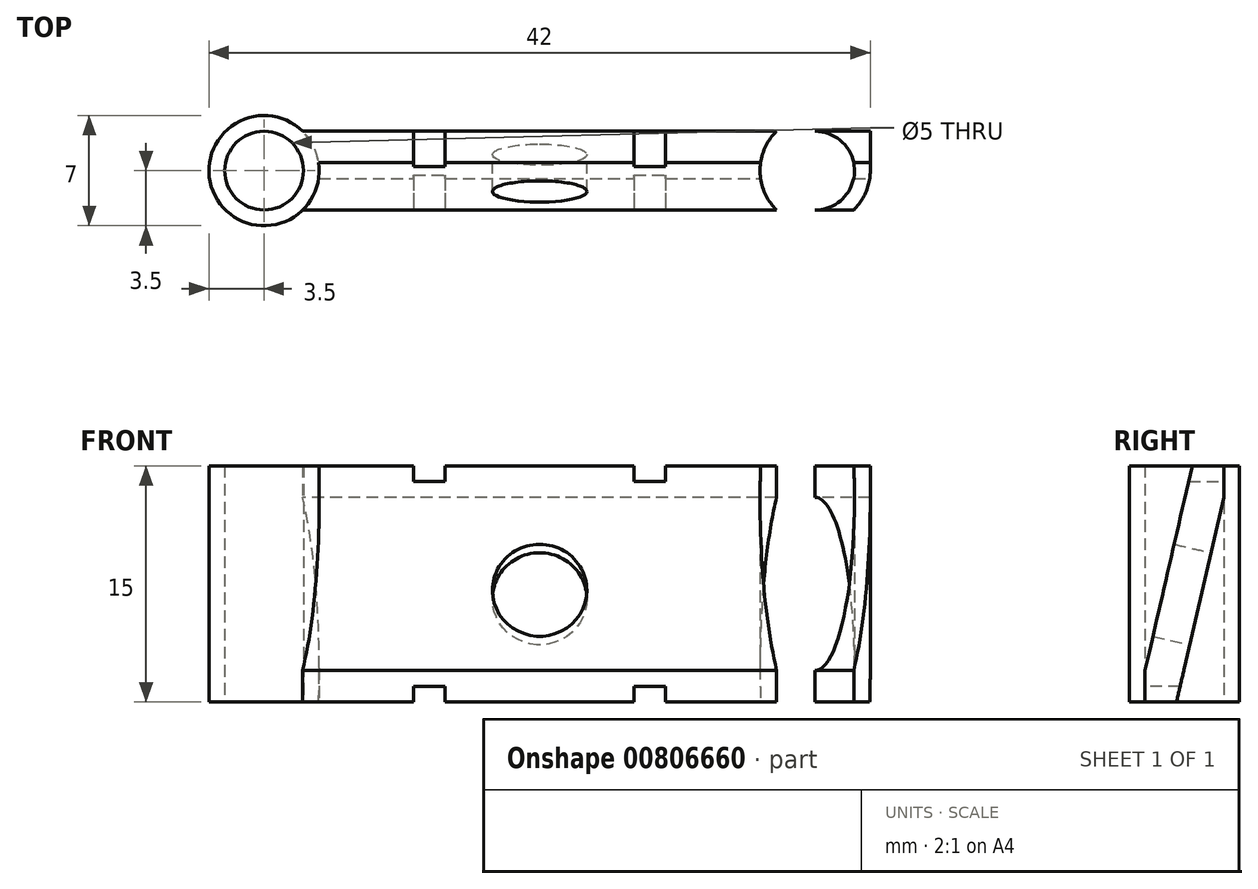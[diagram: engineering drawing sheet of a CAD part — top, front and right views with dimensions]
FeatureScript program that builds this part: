
annotation { "Feature Type Name" : "Feature", "Feature Type Description" : "" }
export const myFeature = defineFeature(function(context is Context, id is Id, definition is map)
    precondition{}
    {
        {
            var Q0;
            Q0=qCreatedBy(makeId("Top.planeOp"),FACE);
            var sketch = newSketch(context, id + "F0", { "sketchPlane" : qUnion([Q0])});
            skLineSegment(sketch, "E0.bottom", {"start": v(21, 2.5) * mm, "end": v(-21, 2.5) * mm});
            skLineSegment(sketch, "E0.top", {"start": v(21, -2.5) * mm, "end": v(-21, -2.5) * mm});
            skLineSegment(sketch, "E0.left", {"start": v(21, 2.5) * mm, "end": v(21, -2.5) * mm});
            skLineSegment(sketch, "E0.right", {"start": v(-21, 2.5) * mm, "end": v(-21, -2.5) * mm});
            skPoint(sketch, "E0.middle", {"position": v(0, 0) * mm});
            skLineSegment(sketch, "E1", {"start": v(-21, 0) * mm, "end": v(21, 0) * mm, "construction": true});
            skLineSegment(sketch, "E2", {"start": v(0, 2.5) * mm, "end": v(0, -2.5) * mm, "construction": true});
            skCircle(sketch, "E3", {"center": v(-17.5, 0) * mm, "radius": 3.5 * mm});
            skCircle(sketch, "E4.MirrorC", {"center": v(17.5, 0) * mm, "radius": 3.5 * mm});
            skCircle(sketch, "E5", {"center": v(-17.5, 0) * mm, "radius": 2.5 * mm});
            skCircle(sketch, "E6.MirrorC", {"center": v(17.5, 0) * mm, "radius": 2.5 * mm});
            skSolve(sketch);
        }
        {
            var Q0;
            {var subQ0=sQuery(id+"F0.wireOp",EDGE,"E3");var subQ1=sQuery(id+"F0.wireOp",EDGE,"E0.bottom");var subQ2=makeQuery(id+"F0.imprint","INTERSECT",VERTEX,{"disambiguationData":[OD(0.0)],"derivedFrom":[subQ1,subQ0]});Q0=makeQuery(id+"F0.imprint","IMPRINT",FACE,{"disambiguationData":[TD([[makeQuery(id+"F0.imprint","IMPRINT",EDGE,{"disambiguationData":[TD([[subQ2,-1.0]])],"derivedFrom":subQ1}),-1.0]])]});}
            var Q1;
            {var subQ0=sQuery(id+"F0.wireOp",EDGE,"E3");var subQ1=sQuery(id+"F0.wireOp",EDGE,"E0.bottom");var subQ2=makeQuery(id+"F0.imprint","INTERSECT",VERTEX,{"disambiguationData":[OD(1.0)],"derivedFrom":[subQ1,subQ0]});Q1=makeQuery(id+"F0.imprint","IMPRINT",FACE,{"disambiguationData":[TD([[makeQuery(id+"F0.imprint","IMPRINT",EDGE,{"disambiguationData":[TD([[subQ2,1.0]])],"derivedFrom":subQ1}),1.0]])]});}
            var Q2;
            {var subQ0=sQuery(id+"F0.wireOp",EDGE,"E3");var subQ1=sQuery(id+"F0.wireOp",EDGE,"E0.top");var subQ2=makeQuery(id+"F0.imprint","INTERSECT",VERTEX,{"disambiguationData":[OD(0.0)],"derivedFrom":[subQ1,subQ0]});Q2=makeQuery(id+"F0.imprint","IMPRINT",FACE,{"disambiguationData":[TD([[makeQuery(id+"F0.imprint","IMPRINT",EDGE,{"disambiguationData":[TD([[subQ2,-1.0]])],"derivedFrom":subQ1}),1.0]])]});}
            var Q3;
            {var subQ0=sQuery(id+"F0.wireOp",EDGE,"E3");var subQ1=sQuery(id+"F0.wireOp",EDGE,"E0.bottom");var subQ2=makeQuery(id+"F0.imprint","INTERSECT",VERTEX,{"disambiguationData":[OD(0.0)],"derivedFrom":[subQ1,subQ0]});Q3=makeQuery(id+"F0.imprint","IMPRINT",FACE,{"disambiguationData":[TD([[makeQuery(id+"F0.imprint","IMPRINT",EDGE,{"disambiguationData":[TD([[subQ2,-1.0]])],"derivedFrom":subQ1}),1.0]])]});}
            var Q4;
            {var subQ0=sQuery(id+"F0.wireOp",EDGE,"E4.MirrorC");var subQ1=sQuery(id+"F0.wireOp",EDGE,"E0.bottom");var subQ2=makeQuery(id+"F0.imprint","INTERSECT",VERTEX,{"disambiguationData":[OD(1.0)],"derivedFrom":[subQ1,subQ0]});Q4=makeQuery(id+"F0.imprint","IMPRINT",FACE,{"disambiguationData":[TD([[makeQuery(id+"F0.imprint","IMPRINT",EDGE,{"disambiguationData":[TD([[subQ2,-1.0]])],"derivedFrom":subQ1}),1.0]])]});}
            var Q5;
            {var subQ0=sQuery(id+"F0.wireOp",EDGE,"E4.MirrorC");var subQ1=sQuery(id+"F0.wireOp",EDGE,"E0.bottom");var subQ2=makeQuery(id+"F0.imprint","INTERSECT",VERTEX,{"disambiguationData":[OD(1.0)],"derivedFrom":[subQ1,subQ0]});Q5=makeQuery(id+"F0.imprint","IMPRINT",FACE,{"disambiguationData":[TD([[makeQuery(id+"F0.imprint","IMPRINT",EDGE,{"disambiguationData":[TD([[subQ2,1.0]])],"derivedFrom":subQ1}),1.0]])]});}
            var Q6;
            {var subQ0=sQuery(id+"F0.wireOp",EDGE,"E4.MirrorC");var subQ1=sQuery(id+"F0.wireOp",EDGE,"E0.bottom");var subQ2=makeQuery(id+"F0.imprint","INTERSECT",VERTEX,{"disambiguationData":[OD(0.0)],"derivedFrom":[subQ1,subQ0]});Q6=makeQuery(id+"F0.imprint","IMPRINT",FACE,{"disambiguationData":[TD([[makeQuery(id+"F0.imprint","IMPRINT",EDGE,{"disambiguationData":[TD([[subQ2,-1.0]])],"derivedFrom":subQ1}),-1.0]])]});}
            var Q7;
            {var subQ0=sQuery(id+"F0.wireOp",EDGE,"E4.MirrorC");var subQ4=sQuery(id+"F0.wireOp",EDGE,"E0.bottom");var subQ5=makeQuery(id+"F0.imprint","INTERSECT",VERTEX,{"disambiguationData":[OD(0.0)],"derivedFrom":[subQ4,subQ0]});Q7=makeQuery(id+"F0.imprint","IMPRINT",FACE,{"disambiguationData":[TD([[makeQuery(id+"F0.imprint","IMPRINT",EDGE,{"disambiguationData":[TD([[subQ5,-1.0]])],"derivedFrom":subQ4}),1.0]])]});}
            var Q8;
            {var subQ0=sQuery(id+"F0.wireOp",EDGE,"E4.MirrorC");var subQ1=sQuery(id+"F0.wireOp",EDGE,"E0.top");var subQ2=makeQuery(id+"F0.imprint","INTERSECT",VERTEX,{"disambiguationData":[OD(0.0)],"derivedFrom":[subQ1,subQ0]});Q8=makeQuery(id+"F0.imprint","IMPRINT",FACE,{"disambiguationData":[TD([[makeQuery(id+"F0.imprint","IMPRINT",EDGE,{"disambiguationData":[TD([[subQ2,-1.0]])],"derivedFrom":subQ1}),1.0]])]});}
            extrude(context, id + "F1", {"entities" : qUnion([Q0, Q1, Q2, Q3, Q4, Q5, Q6, Q7, Q8]), "depth" : 15 * mm, "offsetDistance" : 25 * mm});
        }
        {
            var Q0;
            Q0=makeQuery(id+"F1.opExtrude","CAP_EDGE",EDGE,{"disambiguationData":[OSD([sQuery(id+"F0.wireOp",EDGE,"E0.top")])],"isStart":false});
            chamfer(context, id + "F2", {"entities" : qUnion([Q0]), "chamferType" : ChamferType.TWO_OFFSETS, "width1" : 13 * mm, "oppositeDirection" : false, "width2" : 3 * mm, "tangentPropagation" : true});
        }
        {
            var Q0;
            Q0=makeQuery(id+"F1.opExtrude","CAP_EDGE",EDGE,{"disambiguationData":[OSD([sQuery(id+"F0.wireOp",EDGE,"E0.bottom")])],"isStart":true});
            chamfer(context, id + "F3", {"entities" : qUnion([Q0]), "chamferType" : ChamferType.TWO_OFFSETS, "width1" : 13 * mm, "oppositeDirection" : false, "width2" : 3 * mm, "tangentPropagation" : true});
        }
        {
            var Q0;
            Q0=makeQuery(id+"F3.opChamfer","BLEND_FACE",FACE,{"disambiguationData":[OSD([sQuery(id+"F0.wireOp",EDGE,"E0.bottom")])]});
            var sketch = newSketch(context, id + "F4", { "sketchPlane" : qUnion([Q0])});
            skLineSegment(sketch, "E7", {"start": v(0, 13.23) * mm, "end": v(0, 0) * mm, "construction": true});
            skCircle(sketch, "E8", {"center": v(0, 6.61) * mm, "radius": 3 * mm});
            skSolve(sketch);
        }
        {
            var Q0;
            Q0=makeQuery(id+"F4.imprint","IMPRINT",FACE,{"disambiguationData":[TD([[makeQuery(id+"F4.imprint","IMPRINT",EDGE,{"derivedFrom":sQuery(id+"F4.wireOp",EDGE,"E8")}),1.0]])]});
            extrude(context, id + "F5", {"entities" : qUnion([Q0]), "operationType" : NewBodyOperationType.REMOVE, "oppositeDirection" : true, "depth" : 25 * mm, "offsetDistance" : 25 * mm});
        }
        {
            var Q0;
            Q0=makeQuery(id+"F1.opExtrude","CAP_FACE",FACE,{"disambiguationData":[OSD([sQuery(id+"F0.wireOp",EDGE,"E0.bottom"),sQuery(id+"F0.wireOp",EDGE,"E0.top"),sQuery(id+"F0.wireOp",EDGE,"E3"),sQuery(id+"F0.wireOp",EDGE,"E4.MirrorC"),sQuery(id+"F0.wireOp",EDGE,"E5"),sQuery(id+"F0.wireOp",EDGE,"E6.MirrorC")])],"isStart":false});
            var sketch = newSketch(context, id + "F6", { "sketchPlane" : qUnion([Q0])});
            skLineSegment(sketch, "E9", {"start": v(0, 0.5) * mm, "end": v(0, 2.5) * mm, "construction": true});
            skLineSegment(sketch, "E10.bottom", {"start": v(8, 0) * mm, "end": v(6, 0) * mm});
            skLineSegment(sketch, "E10.top", {"start": v(8, 3) * mm, "end": v(6, 3) * mm});
            skLineSegment(sketch, "E10.left", {"start": v(8, 0) * mm, "end": v(8, 3) * mm});
            skLineSegment(sketch, "E10.right", {"start": v(6, 0) * mm, "end": v(6, 3) * mm});
            skLineSegment(sketch, "E11.MirrorCS", {"start": v(-6, 0) * mm, "end": v(-6, 3) * mm});
            skLineSegment(sketch, "E12.MirrorCS", {"start": v(-8, 0) * mm, "end": v(-8, 3) * mm});
            skLineSegment(sketch, "E13.MirrorCS", {"start": v(-8, 3) * mm, "end": v(-6, 3) * mm});
            skLineSegment(sketch, "E14.MirrorCS", {"start": v(-8, 0) * mm, "end": v(-6, 0) * mm});
            skLineSegment(sketch, "E15", {"start": v(8, 1.5) * mm, "end": v(6, 1.5) * mm, "construction": true});
            skLineSegment(sketch, "E16", {"start": v(0, 1.5) * mm, "end": v(14.82, 1.5) * mm, "construction": true});
            skSolve(sketch);
        }
        {
            var Q0;
            Q0=makeQuery(id+"F6.imprint","IMPRINT",FACE,{"disambiguationData":[TD([[makeQuery(id+"F6.imprint","IMPRINT",EDGE,{"derivedFrom":sQuery(id+"F6.wireOp",EDGE,"E10.bottom")}),1.0]])]});
            var Q1;
            Q1=makeQuery(id+"F6.imprint","IMPRINT",FACE,{"disambiguationData":[TD([[makeQuery(id+"F6.imprint","IMPRINT",EDGE,{"derivedFrom":sQuery(id+"F6.wireOp",EDGE,"E11.MirrorCS")}),1.0]])]});
            var Q2;
            {var subQ0=sQuery(id+"F6.wireOp",EDGE,"E10.left");var subQ2=sQuery(id+"F0.wireOp",EDGE,"E0.bottom");var subQ5=makeQuery(id+"F1.opExtrude","CAP_EDGE",EDGE,{"disambiguationData":[OSD([subQ2])],"isStart":false});var subQ6=makeQuery(id+"F6.imprint","INTERSECT",VERTEX,{"derivedFrom":[subQ5,subQ0]});Q2=makeQuery(id+"F6.imprint","IMPRINT",FACE,{"disambiguationData":[TD([[makeQuery(id+"F6.imprint","IMPRINT",EDGE,{"disambiguationData":[TD([[subQ6,-1.0]])],"derivedFrom":subQ5}),1.0]])]});}
            var Q3;
            {var subQ0=sQuery(id+"F6.wireOp",EDGE,"E10.bottom");Q3=makeQuery(id+"F6.imprint","IMPRINT",FACE,{"disambiguationData":[TD([[makeQuery(id+"F6.imprint","IMPRINT",EDGE,{"derivedFrom":subQ0}),-1.0]])]});}
            var Q4;
            {var subQ0=sQuery(id+"F6.wireOp",EDGE,"E10.top");Q4=makeQuery(id+"F6.imprint","IMPRINT",FACE,{"disambiguationData":[TD([[makeQuery(id+"F6.imprint","IMPRINT",EDGE,{"derivedFrom":subQ0}),1.0]])]});}
            extrude(context, id + "F7", {"entities" : qUnion([Q0, Q1, Q2, Q3, Q4]), "operationType" : NewBodyOperationType.REMOVE, "oppositeDirection" : true, "depth" : 1 * mm, "offsetDistance" : 25 * mm});
        }
        {
            var Q0;
            Q0=makeQuery(id+"F1.opExtrude","CAP_FACE",FACE,{"disambiguationData":[OSD([sQuery(id+"F0.wireOp",EDGE,"E0.bottom"),sQuery(id+"F0.wireOp",EDGE,"E0.top"),sQuery(id+"F0.wireOp",EDGE,"E3"),sQuery(id+"F0.wireOp",EDGE,"E4.MirrorC"),sQuery(id+"F0.wireOp",EDGE,"E5"),sQuery(id+"F0.wireOp",EDGE,"E6.MirrorC")])],"isStart":true});
            var sketch = newSketch(context, id + "F8", { "sketchPlane" : qUnion([Q0])});
            skLineSegment(sketch, "E17", {"start": v(0, 0.5) * mm, "end": v(0, 2.5) * mm, "construction": true});
            skLineSegment(sketch, "E18", {"start": v(0, 1.5) * mm, "end": v(15.17, 1.5) * mm, "construction": true});
            skLineSegment(sketch, "E19.bottom", {"start": v(8, 0) * mm, "end": v(6, 0) * mm});
            skLineSegment(sketch, "E19.top", {"start": v(8, 3) * mm, "end": v(6, 3) * mm});
            skLineSegment(sketch, "E19.left", {"start": v(8, 0) * mm, "end": v(8, 3) * mm});
            skLineSegment(sketch, "E19.right", {"start": v(6, 0) * mm, "end": v(6, 3) * mm});
            skLineSegment(sketch, "E20", {"start": v(8, 1.5) * mm, "end": v(6, 1.5) * mm, "construction": true});
            skLineSegment(sketch, "E21.MirrorCS", {"start": v(-8, 1.5) * mm, "end": v(-6, 1.5) * mm, "construction": true});
            skLineSegment(sketch, "E22.MirrorCS", {"start": v(-8, 0) * mm, "end": v(-6, 0) * mm});
            skLineSegment(sketch, "E23.MirrorCS", {"start": v(-8, 0) * mm, "end": v(-8, 3) * mm});
            skLineSegment(sketch, "E24.MirrorCS", {"start": v(-6, 0) * mm, "end": v(-6, 3) * mm});
            skLineSegment(sketch, "E25.MirrorCS", {"start": v(-8, 3) * mm, "end": v(-6, 3) * mm});
            skSolve(sketch);
        }
        {
            var Q0;
            {var subQ0=sQuery(id+"F8.wireOp",EDGE,"E19.bottom");Q0=makeQuery(id+"F8.imprint","IMPRINT",FACE,{"disambiguationData":[TD([[makeQuery(id+"F8.imprint","IMPRINT",EDGE,{"derivedFrom":subQ0}),-1.0]])]});}
            var Q1;
            {var subQ0=sQuery(id+"F8.wireOp",EDGE,"E19.left");var subQ1=sQuery(id+"F0.wireOp",EDGE,"E0.top");var subQ5=makeQuery(id+"F1.opExtrude","CAP_EDGE",EDGE,{"disambiguationData":[OSD([subQ1])],"isStart":true});var subQ6=makeQuery(id+"F8.imprint","INTERSECT",VERTEX,{"derivedFrom":[subQ5,subQ0]});Q1=makeQuery(id+"F8.imprint","IMPRINT",FACE,{"disambiguationData":[TD([[makeQuery(id+"F8.imprint","IMPRINT",EDGE,{"disambiguationData":[TD([[subQ6,-1.0]])],"derivedFrom":subQ5}),1.0]])]});}
            var Q2;
            {var subQ0=sQuery(id+"F8.wireOp",EDGE,"E19.top");Q2=makeQuery(id+"F8.imprint","IMPRINT",FACE,{"disambiguationData":[TD([[makeQuery(id+"F8.imprint","IMPRINT",EDGE,{"derivedFrom":subQ0}),1.0]])]});}
            var Q3;
            {var subQ0=sQuery(id+"F8.wireOp",EDGE,"E22.MirrorCS");Q3=makeQuery(id+"F8.imprint","IMPRINT",FACE,{"disambiguationData":[TD([[makeQuery(id+"F8.imprint","IMPRINT",EDGE,{"derivedFrom":subQ0}),1.0]])]});}
            var Q4;
            {var subQ0=sQuery(id+"F8.wireOp",EDGE,"E23.MirrorCS");var subQ1=sQuery(id+"F0.wireOp",EDGE,"E0.top");var subQ5=makeQuery(id+"F1.opExtrude","CAP_EDGE",EDGE,{"disambiguationData":[OSD([subQ1])],"isStart":true});var subQ6=makeQuery(id+"F8.imprint","INTERSECT",VERTEX,{"derivedFrom":[subQ5,subQ0]});Q4=makeQuery(id+"F8.imprint","IMPRINT",FACE,{"disambiguationData":[TD([[makeQuery(id+"F8.imprint","IMPRINT",EDGE,{"disambiguationData":[TD([[subQ6,1.0]])],"derivedFrom":subQ5}),1.0]])]});}
            var Q5;
            {var subQ0=sQuery(id+"F8.wireOp",EDGE,"E25.MirrorCS");Q5=makeQuery(id+"F8.imprint","IMPRINT",FACE,{"disambiguationData":[TD([[makeQuery(id+"F8.imprint","IMPRINT",EDGE,{"derivedFrom":subQ0}),-1.0]])]});}
            extrude(context, id + "F9", {"entities" : qUnion([Q0, Q1, Q2, Q3, Q4, Q5]), "operationType" : NewBodyOperationType.REMOVE, "oppositeDirection" : true, "depth" : 1 * mm, "offsetDistance" : 25 * mm});
        }
    });
